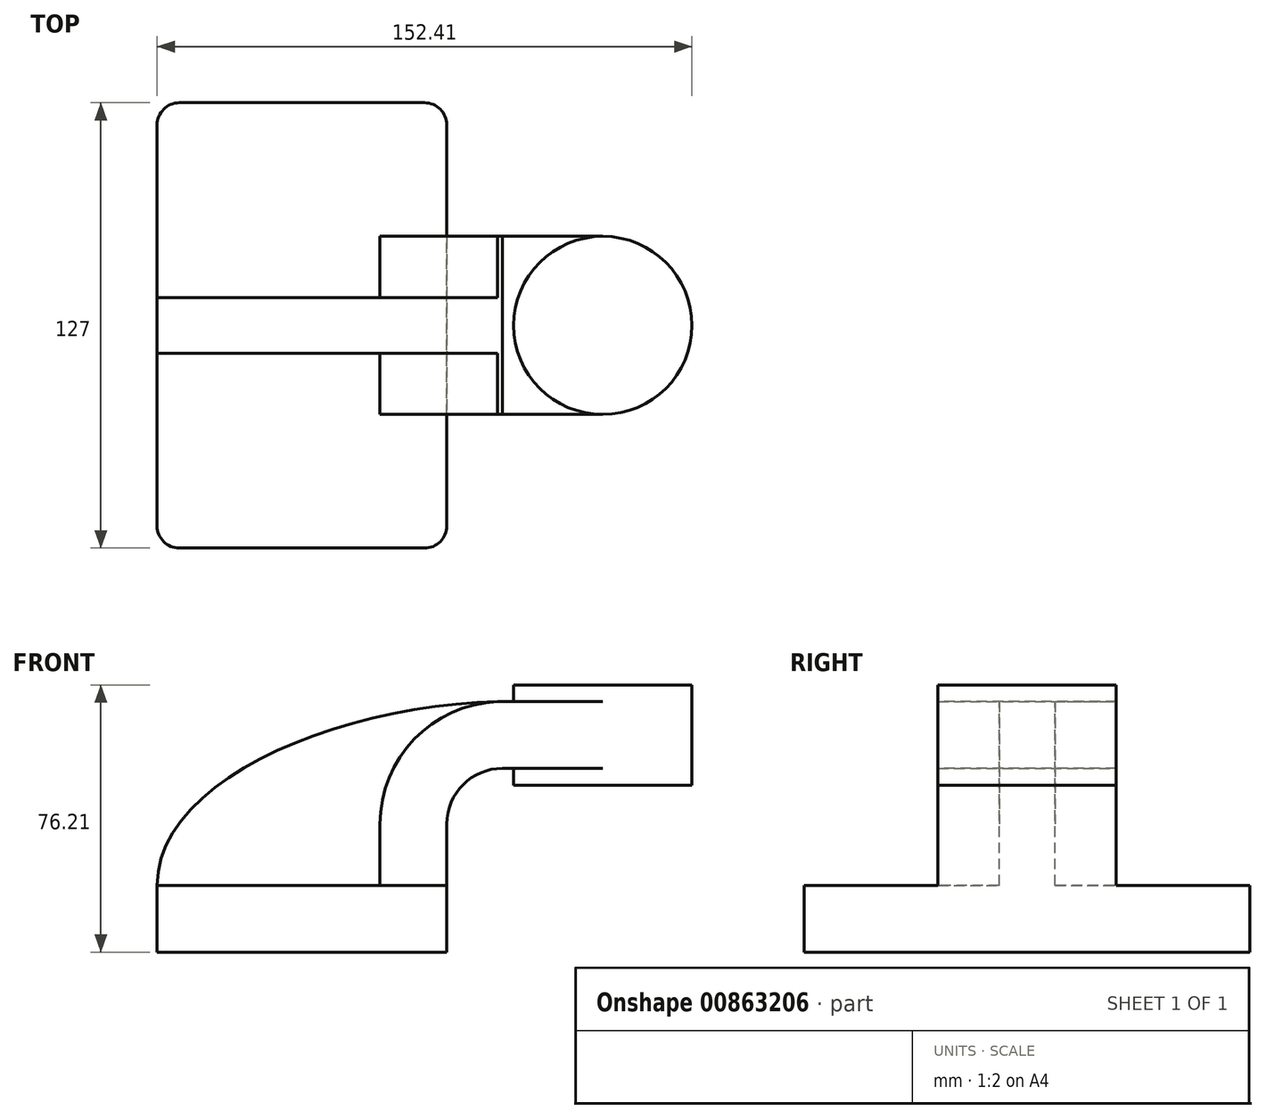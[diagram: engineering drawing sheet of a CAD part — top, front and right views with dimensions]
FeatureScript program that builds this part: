
annotation { "Feature Type Name" : "Feature", "Feature Type Description" : "" }
export const myFeature = defineFeature(function(context is Context, id is Id, definition is map)
    precondition{}
    {
        {
            var Q0;
            Q0=qCreatedBy(makeId("Front.planeOp"),FACE);
            var sketch = newSketch(context, id + "F0", { "sketchPlane" : qUnion([Q0])});
            skLineSegment(sketch, "E0.bottom", {"start": v(41.28, 9.53) * mm, "end": v(-41.28, 9.53) * mm});
            skLineSegment(sketch, "E0.top", {"start": v(41.28, -9.52) * mm, "end": v(-41.28, -9.52) * mm});
            skLineSegment(sketch, "E0.left", {"start": v(41.28, 9.53) * mm, "end": v(41.28, -9.52) * mm});
            skLineSegment(sketch, "E0.right", {"start": v(-41.28, 9.53) * mm, "end": v(-41.28, -9.52) * mm});
            skPoint(sketch, "E0.middle", {"position": v(0, 0) * mm});
            skLineSegment(sketch, "E1.bottom", {"start": v(60.32, 38.1) * mm, "end": v(111.12, 38.1) * mm});
            skLineSegment(sketch, "E1.top", {"start": v(60.32, 66.68) * mm, "end": v(111.12, 66.68) * mm});
            skLineSegment(sketch, "E1.left", {"start": v(60.32, 38.1) * mm, "end": v(60.32, 66.68) * mm});
            skLineSegment(sketch, "E1.right", {"start": v(111.12, 38.1) * mm, "end": v(111.12, 66.68) * mm});
            skPoint(sketch, "E1.middle", {"position": v(85.72, 52.39) * mm});
            skLineSegment(sketch, "E2", {"start": v(41.28, 9.53) * mm, "end": v(41.28, 27) * mm});
            skArc(sketch, "E3", {"start": v(41.27, 27) * mm, "mid": v(45.92, 38.23) * mm, "end": v(57.15, 42.88) * mm});
            skLineSegment(sketch, "E4", {"start": v(57.15, 42.88) * mm, "end": v(85.72, 42.88) * mm});
            skLineSegment(sketch, "E5.0", {"start": v(57.15, 61.93) * mm, "end": v(85.72, 61.93) * mm});
            skArc(sketch, "E5.1", {"start": v(22.22, 27) * mm, "mid": v(32.45, 51.7) * mm, "end": v(57.15, 61.93) * mm});
            skLineSegment(sketch, "E5.2", {"start": v(22.22, 9.53) * mm, "end": v(22.22, 27) * mm});
            skLineSegment(sketch, "E6", {"start": v(85.72, 66.68) * mm, "end": v(85.72, 38.1) * mm});
            skFitSpline(sketch, "E7", {"points": [v(-41.28, 9.53) * mm, v(57.15, 61.93) * mm], "startDerivative": vector(0.37, 92.32) * mm, "endDerivative": vector(135.74, 2.07) * mm});
            skSolve(sketch);
        }
        {
            var Q0;
            Q0=makeQuery(id+"F0.imprint","IMPRINT",FACE,{"disambiguationData":[TD([[makeQuery(id+"F0.imprint","IMPRINT",EDGE,{"derivedFrom":sQuery(id+"F0.wireOp",EDGE,"E0.top")}),-1.0]])]});
            extrude(context, id + "F1", {"entities" : qUnion([Q0]), "endBound" : BoundingType.SYMMETRIC, "oppositeDirection" : true, "depth" : 127 * mm, "offsetDistance" : 25.4 * mm, "hasSecondDirection" : true, "secondDirectionOppositeDirection" : false, "secondDirectionDepth" : 25.4 * mm});
        }
        {
            var Q0;
            {var subQ0=sQuery(id+"F0.wireOp",EDGE,"E4");var subQ1=sQuery(id+"F0.wireOp",EDGE,"E1.left");var subQ2=makeQuery(id+"F0.imprint","INTERSECT",VERTEX,{"derivedFrom":[subQ1,subQ0]});Q0=makeQuery(id+"F0.imprint","IMPRINT",FACE,{"disambiguationData":[TD([[makeQuery(id+"F0.imprint","IMPRINT",EDGE,{"disambiguationData":[TD([[subQ2,-1.0]])],"derivedFrom":subQ1}),-1.0]])]});}
            var Q1;
            {var subQ1=sQuery(id+"F0.wireOp",EDGE,"E2");Q1=makeQuery(id+"F0.imprint","IMPRINT",FACE,{"disambiguationData":[TD([[makeQuery(id+"F0.imprint","IMPRINT",EDGE,{"derivedFrom":subQ1}),1.0]])]});}
            extrude(context, id + "F2", {"entities" : qUnion([Q0, Q1]), "operationType" : NewBodyOperationType.ADD, "endBound" : BoundingType.SYMMETRIC, "depth" : 50.8 * mm, "offsetDistance" : 25.4 * mm});
        }
        {
            var Q0;
            {var subQ3=sQuery(id+"F0.wireOp",EDGE,"E5.2");Q0=makeQuery(id+"F0.imprint","IMPRINT",FACE,{"disambiguationData":[TD([[makeQuery(id+"F0.imprint","IMPRINT",EDGE,{"derivedFrom":subQ3}),1.0]])]});}
            extrude(context, id + "F3", {"entities" : qUnion([Q0]), "operationType" : NewBodyOperationType.ADD, "endBound" : BoundingType.SYMMETRIC, "depth" : 15.88 * mm, "offsetDistance" : 25.4 * mm});
        }
        {
            var Q0;
            {var subQ4=sQuery(id+"F0.wireOp",EDGE,"E1.right");Q0=makeQuery(id+"F0.imprint","IMPRINT",FACE,{"disambiguationData":[TD([[makeQuery(id+"F0.imprint","IMPRINT",EDGE,{"derivedFrom":subQ4}),1.0]])]});}
            var Q1;
            Q1=sQuery(id+"F0.wireOp",EDGE,"E6");
            revolve(context, id + "F4", {"operationType" : NewBodyOperationType.ADD, "surfaceOperationType" : NewSurfaceOperationType.NEW, "entities" : qUnion([Q0]), "axis" : qUnion([Q1]), "revolveType" : RevolveType.FULL});
        }
        {
            var Q0;
            Q0=makeQuery(id+"F1.opExtrude","CAP_EDGE",EDGE,{"disambiguationData":[OSD([sQuery(id+"F0.wireOp",EDGE,"E0.left")])],"isStart":true});
            var Q1;
            Q1=makeQuery(id+"F1.opExtrude","CAP_EDGE",EDGE,{"disambiguationData":[OSD([sQuery(id+"F0.wireOp",EDGE,"E0.right")])],"isStart":true});
            var Q2;
            Q2=makeQuery(id+"F1.opExtrude","CAP_EDGE",EDGE,{"disambiguationData":[OSD([sQuery(id+"F0.wireOp",EDGE,"E0.left")])],"isStart":false});
            var Q3;
            Q3=makeQuery(id+"F1.opExtrude","CAP_EDGE",EDGE,{"disambiguationData":[OSD([sQuery(id+"F0.wireOp",EDGE,"E0.right")])],"isStart":false});
            fillet(context, id + "F5", {"entities" : qUnion([Q0, Q1, Q2, Q3]), "radius" : 6.35 * mm, "tangentPropagation" : true, "allowEdgeOverflow" : false});
        }
    });
